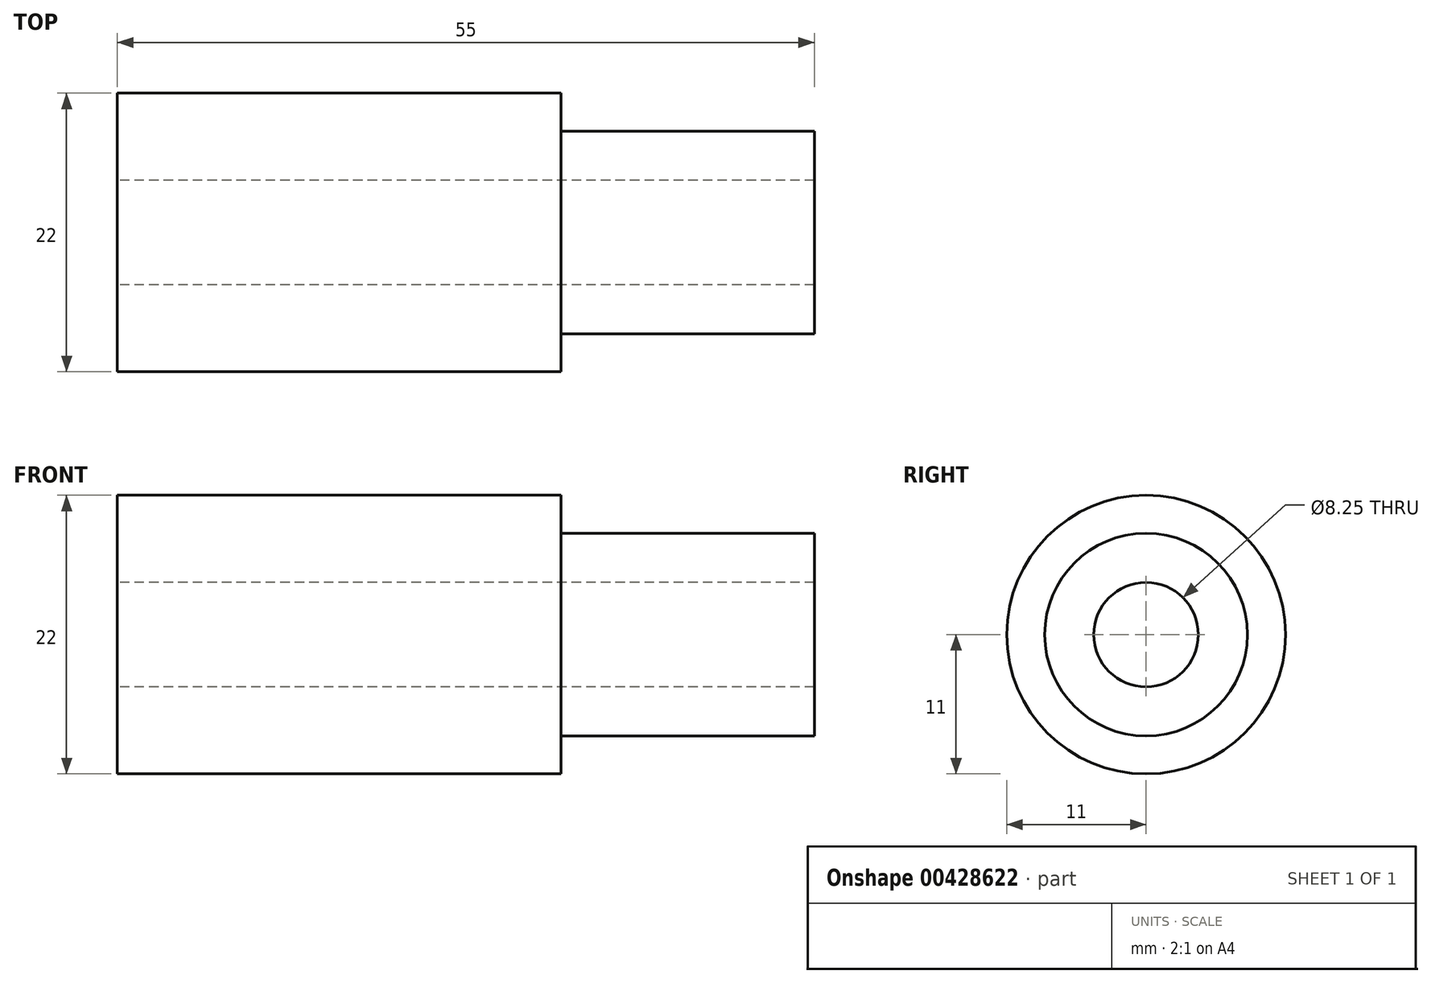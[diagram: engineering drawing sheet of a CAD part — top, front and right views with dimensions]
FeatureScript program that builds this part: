
annotation { "Feature Type Name" : "Feature", "Feature Type Description" : "" }
export const myFeature = defineFeature(function(context is Context, id is Id, definition is map)
    precondition{}
    {
        {
            var Q0;
            Q0=qCreatedBy(makeId("Top.planeOp"),FACE);
            var sketch = newSketch(context, id + "F0", { "sketchPlane" : qUnion([Q0])});
            skLineSegment(sketch, "E0.0", {"start": v(0, 11) * mm, "end": v(35, 11) * mm});
            skLineSegment(sketch, "E1", {"start": v(0, 11) * mm, "end": v(0, 4.12) * mm});
            skLineSegment(sketch, "E2.0", {"start": v(35, 11) * mm, "end": v(35, 8) * mm});
            skLineSegment(sketch, "E3.0", {"start": v(35, 8) * mm, "end": v(55, 8) * mm});
            skLineSegment(sketch, "E4.0", {"start": v(55, 8) * mm, "end": v(55, 4.12) * mm});
            skLineSegment(sketch, "E5.0", {"start": v(0, 4.12) * mm, "end": v(55, 4.12) * mm});
            skLineSegment(sketch, "E6", {"start": v(0, 0) * mm, "end": v(61.35, 0) * mm, "construction": true});
            skSolve(sketch);
        }
        {
            var Q0;
            Q0=makeQuery(id+"F0.imprint","IMPRINT",FACE,{"disambiguationData":[TD([[makeQuery(id+"F0.imprint","IMPRINT",EDGE,{"derivedFrom":sQuery(id+"F0.wireOp",EDGE,"E0.0")}),-1.0]])]});
            var Q1;
            Q1=sQuery(id+"F0.wireOp",EDGE,"E6");
            revolve(context, id + "F1", {"entities" : qUnion([Q0]), "axis" : qUnion([Q1]), "revolveType" : RevolveType.FULL});
        }
    });
